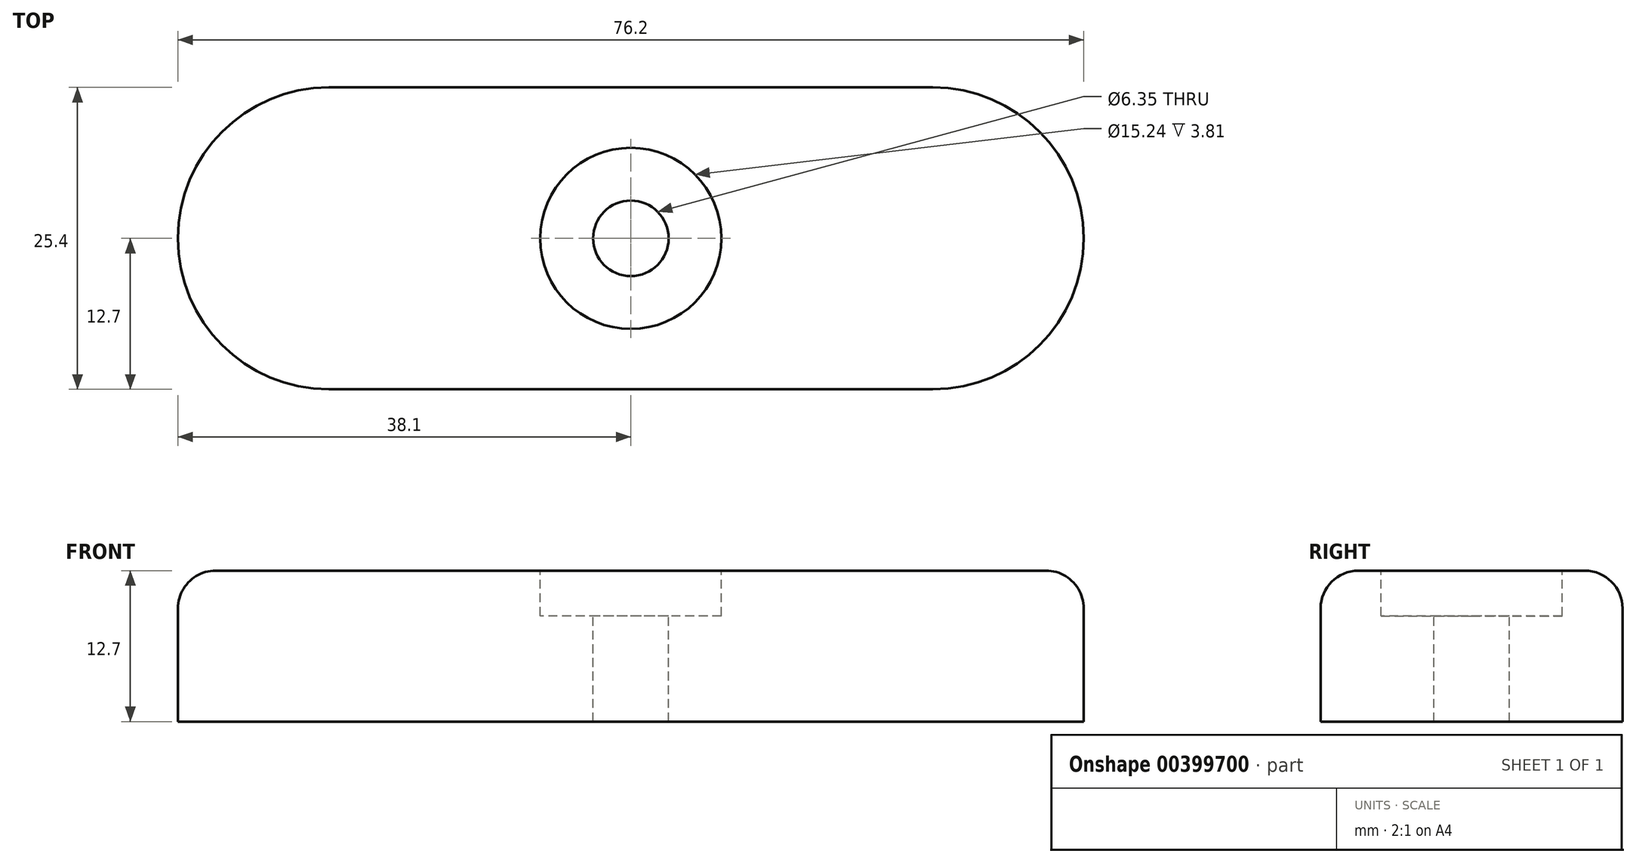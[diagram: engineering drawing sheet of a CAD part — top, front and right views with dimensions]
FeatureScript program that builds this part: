
annotation { "Feature Type Name" : "Feature", "Feature Type Description" : "" }
export const myFeature = defineFeature(function(context is Context, id is Id, definition is map)
    precondition{}
    {
        {
            var Q0;
            Q0=qCreatedBy(makeId("Top.planeOp"),FACE);
            var sketch = newSketch(context, id + "F0", { "sketchPlane" : qUnion([Q0])});
            skLineSegment(sketch, "E0.bottom", {"start": v(-25.4, 12.7) * mm, "end": v(25.4, 12.7) * mm});
            skLineSegment(sketch, "E0.top", {"start": v(-25.4, -12.7) * mm, "end": v(25.4, -12.7) * mm});
            skLineSegment(sketch, "E0.left", {"start": v(-25.4, 12.7) * mm, "end": v(-25.4, -12.7) * mm});
            skLineSegment(sketch, "E0.right", {"start": v(25.4, 12.7) * mm, "end": v(25.4, -12.7) * mm});
            skArc(sketch, "E1", {"start": v(-25.4, 12.7) * mm, "mid": v(-38.1, 0) * mm, "end": v(-25.4, -12.7) * mm});
            skArc(sketch, "E2", {"start": v(25.4, 12.7) * mm, "mid": v(38.1, 0) * mm, "end": v(25.4, -12.7) * mm});
            skSolve(sketch);
        }
        {
            var Q0;
            Q0=makeQuery(id+"F0.imprint","IMPRINT",FACE,{"disambiguationData":[TD([[makeQuery(id+"F0.imprint","IMPRINT",EDGE,{"derivedFrom":sQuery(id+"F0.wireOp",EDGE,"E0.bottom")}),-1.0]])]});
            var Q1;
            Q1=makeQuery(id+"F0.imprint","IMPRINT",FACE,{"disambiguationData":[TD([[makeQuery(id+"F0.imprint","IMPRINT",EDGE,{"derivedFrom":sQuery(id+"F0.wireOp",EDGE,"E0.left")}),-1.0]])]});
            var Q2;
            Q2=makeQuery(id+"F0.imprint","IMPRINT",FACE,{"disambiguationData":[TD([[makeQuery(id+"F0.imprint","IMPRINT",EDGE,{"derivedFrom":sQuery(id+"F0.wireOp",EDGE,"E0.right")}),1.0]])]});
            extrude(context, id + "F1", {"entities" : qUnion([Q0, Q1, Q2]), "depth" : 12.7 * mm});
        }
        {
            var Q0;
            Q0=makeQuery(id+"F1.opExtrude","CAP_FACE",FACE,{"disambiguationData":[OSD([sQuery(id+"F0.wireOp",EDGE,"E0.bottom"),sQuery(id+"F0.wireOp",EDGE,"E0.top"),sQuery(id+"F0.wireOp",EDGE,"E1"),sQuery(id+"F0.wireOp",EDGE,"E2")])],"isStart":false});
            var sketch = newSketch(context, id + "F2", { "sketchPlane" : qUnion([Q0])});
            skPoint(sketch, "E3", {"position": v(0, 0) * mm});
            skSolve(sketch);
        }
        {
            var Q0;
            Q0=sQuery(id+"F2.wireOp",VERTEX,"E3");
            var Q1;
            Q1=makeQuery(id+"F1.opExtrude","SWEPT_BODY",BODY,{"disambiguationData":[OSD([sQuery(id+"F0.wireOp",EDGE,"E0.bottom"),sQuery(id+"F0.wireOp",EDGE,"E0.top"),sQuery(id+"F0.wireOp",EDGE,"E1"),sQuery(id+"F0.wireOp",EDGE,"E2")])]});
            hole(context, id + "F3", {"style" : HoleStyle.C_BORE, "endStyle" : HoleEndStyle.THROUGH, "holeDiameter" : 6.35 * mm, "cBoreDiameter" : 15.24 * mm, "cBoreDepth" : 3.8 * mm, "isTappedThrough" : true, "tappedDepth" : 12.7 * mm, "tapClearance" : 3, "locations" : qUnion([Q0]), "scope" : qUnion([Q1])});
        }
        {
            var Q0;
            Q0=makeQuery(id+"F1.opExtrude","CAP_EDGE",EDGE,{"disambiguationData":[OSD([sQuery(id+"F0.wireOp",EDGE,"E1")])],"isStart":false});
            fillet(context, id + "F4", {"entities" : qUnion([Q0]), "radius" : 3.17 * mm, "tangentPropagation" : true, "allowEdgeOverflow" : false});
        }
    });
